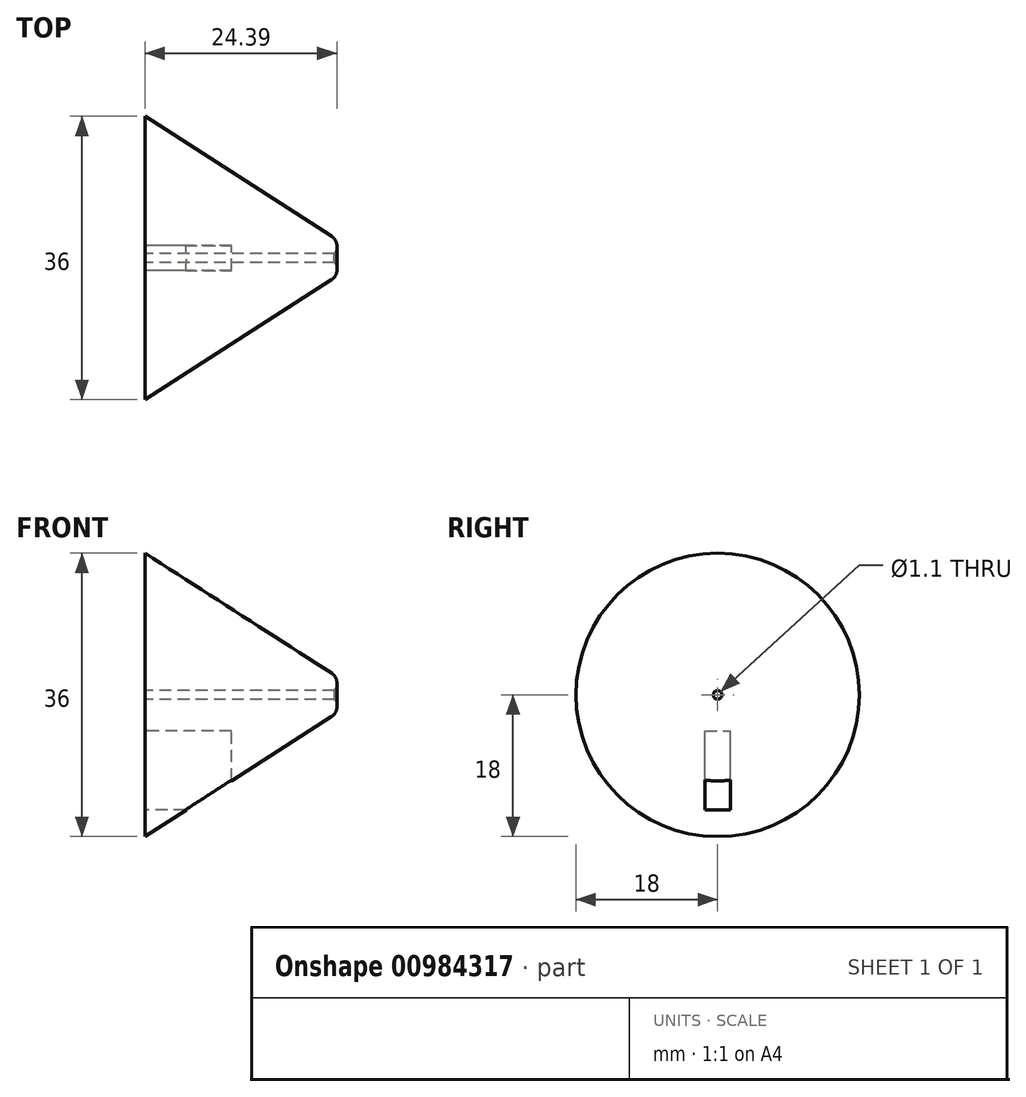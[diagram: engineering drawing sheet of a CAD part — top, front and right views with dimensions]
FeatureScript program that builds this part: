
annotation { "Feature Type Name" : "Feature", "Feature Type Description" : "" }
export const myFeature = defineFeature(function(context is Context, id is Id, definition is map)
    precondition{}
    {
        {
            var Q0;
            Q0=qCreatedBy(makeId("Front.planeOp"),FACE);
            var sketch = newSketch(context, id + "F0", { "sketchPlane" : qUnion([Q0])});
            skLineSegment(sketch, "E0", {"start": v(0, 0) * mm, "end": v(22.9, 0) * mm});
            skLineSegment(sketch, "E1", {"start": v(23.7, 2.76) * mm, "end": v(0, 18) * mm});
            skLineSegment(sketch, "E2", {"start": v(0, 18) * mm, "end": v(0, 0) * mm});
            skPoint(sketch, "E3.visualSharp", {"position": v(28, 0) * mm});
            skArc(sketch, "E3.filletArc", {"start": v(22.9, 0) * mm, "mid": v(24.33, 1.08) * mm, "end": v(23.7, 2.76) * mm});
            skSolve(sketch);
        }
        {
            var Q0;
            Q0=makeQuery(id+"F0.imprint","IMPRINT",FACE,{"disambiguationData":[TD([[makeQuery(id+"F0.imprint","IMPRINT",EDGE,{"derivedFrom":sQuery(id+"F0.wireOp",EDGE,"E0")}),1.0]])]});
            var Q1;
            Q1=sQuery(id+"F0.wireOp",EDGE,"E0");
            revolve(context, id + "F1", {"surfaceOperationType" : NewSurfaceOperationType.NEW, "entities" : qUnion([Q0]), "axis" : qUnion([Q1]), "revolveType" : RevolveType.FULL});
        }
        {
            var Q0;
            Q0=qCreatedBy(makeId("Right.planeOp"),FACE);
            var sketch = newSketch(context, id + "F2", { "sketchPlane" : qUnion([Q0])});
            skCircle(sketch, "E4", {"center": v(0, 0) * mm, "radius": 0.75 * mm});
            skSolve(sketch);
        }
        {
            var Q0;
            Q0=sQuery(id+"F2.wireOp",VERTEX,"E4.center");
            var Q1;
            Q1=makeQuery(id+"F1.opRevolve","SWEPT_BODY",BODY,{"disambiguationData":[OSD([sQuery(id+"F0.wireOp",EDGE,"E0"),sQuery(id+"F0.wireOp",EDGE,"E1"),sQuery(id+"F0.wireOp",EDGE,"E2")])]});
            hole(context, id + "F3", {"style" : HoleStyle.SIMPLE, "endStyle" : HoleEndStyle.THROUGH, "oppositeDirection" : true, "holeDiameter" : 1.1 * mm, "majorDiameter" : 5 * mm, "isTappedThrough" : true, "tappedDepth" : 12 * mm, "tapClearance" : 3, "locations" : qUnion([Q0]), "scope" : qUnion([Q1])});
        }
        {
            var Q0;
            Q0=qCreatedBy(makeId("Right.planeOp"),FACE);
            var sketch = newSketch(context, id + "F4", { "sketchPlane" : qUnion([Q0])});
            skLineSegment(sketch, "E5.bottom", {"start": v(-1.6, -14.6) * mm, "end": v(1.6, -14.6) * mm});
            skLineSegment(sketch, "E5.top", {"start": v(-1.6, -4.6) * mm, "end": v(1.6, -4.6) * mm});
            skLineSegment(sketch, "E5.left", {"start": v(-1.6, -14.6) * mm, "end": v(-1.6, -8.85) * mm});
            skLineSegment(sketch, "E5.right", {"start": v(1.6, -14.6) * mm, "end": v(1.6, -8.85) * mm});
            skPoint(sketch, "E5.middle", {"position": v(0, -9.6) * mm});
            skLineSegment(sketch, "E6.trimOffspring", {"start": v(-1.6, -8.85) * mm, "end": v(-1.6, -4.6) * mm});
            skLineSegment(sketch, "E7.trimOffspring", {"start": v(1.6, -8.85) * mm, "end": v(1.6, -4.6) * mm});
            skSolve(sketch);
        }
        {
            var Q0;
            Q0 = qSketchRegion(id + "F4", true);
            extrude(context, id + "F5", {"entities" : qUnion([Q0]), "operationType" : NewBodyOperationType.REMOVE, "depth" : 11 * mm, "offsetDistance" : 25 * mm});
        }
    });
